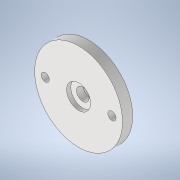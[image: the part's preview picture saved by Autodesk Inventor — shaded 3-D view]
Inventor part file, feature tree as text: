
AUTODESK INVENTOR PART (.ipt)
format: ipt  version: 2022 (Build 260153000, 153)  size: 135,680 bytes
history: native  units: mm
features: extrude x5, sketch x5, reference x2, other x2
ambient origin geometry x8: Origin, YZ Plane, XZ Plane, XY Plane, X Axis, Y Axis, Z Axis, Center Point
bodies: Solid1 (feature_tree)
feature tree (14):
  extrude  "Extrusion1"  Depth=2.4mm TaperAngle=0.0deg
  extrude  "Extrusion2"  Depth=5.4mm
  extrude  "Extrusion3"  Depth=3.0mm
  extrude  "Extrusion4"  Depth=2.1mm
  extrude  "Extrusion5"  Depth=3.0mm
  sketch  "Sketch3"  dims[d0=20.8mm d1=2.4mm d2=0.0mm]
  reference  "Reference1"
  reference  "Reference2"
  sketch  "Sketch4"  dims[d3=8.7mm d4=5.4mm]
  sketch  "Sketch5"  dims[d5=3.0mm d6=0.0mm d7=5.5mm]
  sketch  "Sketch6"  dims[d8=2.1mm d9=0.0mm d10=5.7mm]
  sketch  "Sketch7"  dims[d11=1.0mm d12=0.0mm d13=3.0mm d14=0.0mm d15=0.0mm]
  other  "EnsambleCuerpo.iam"
  other  "Base3:1"
